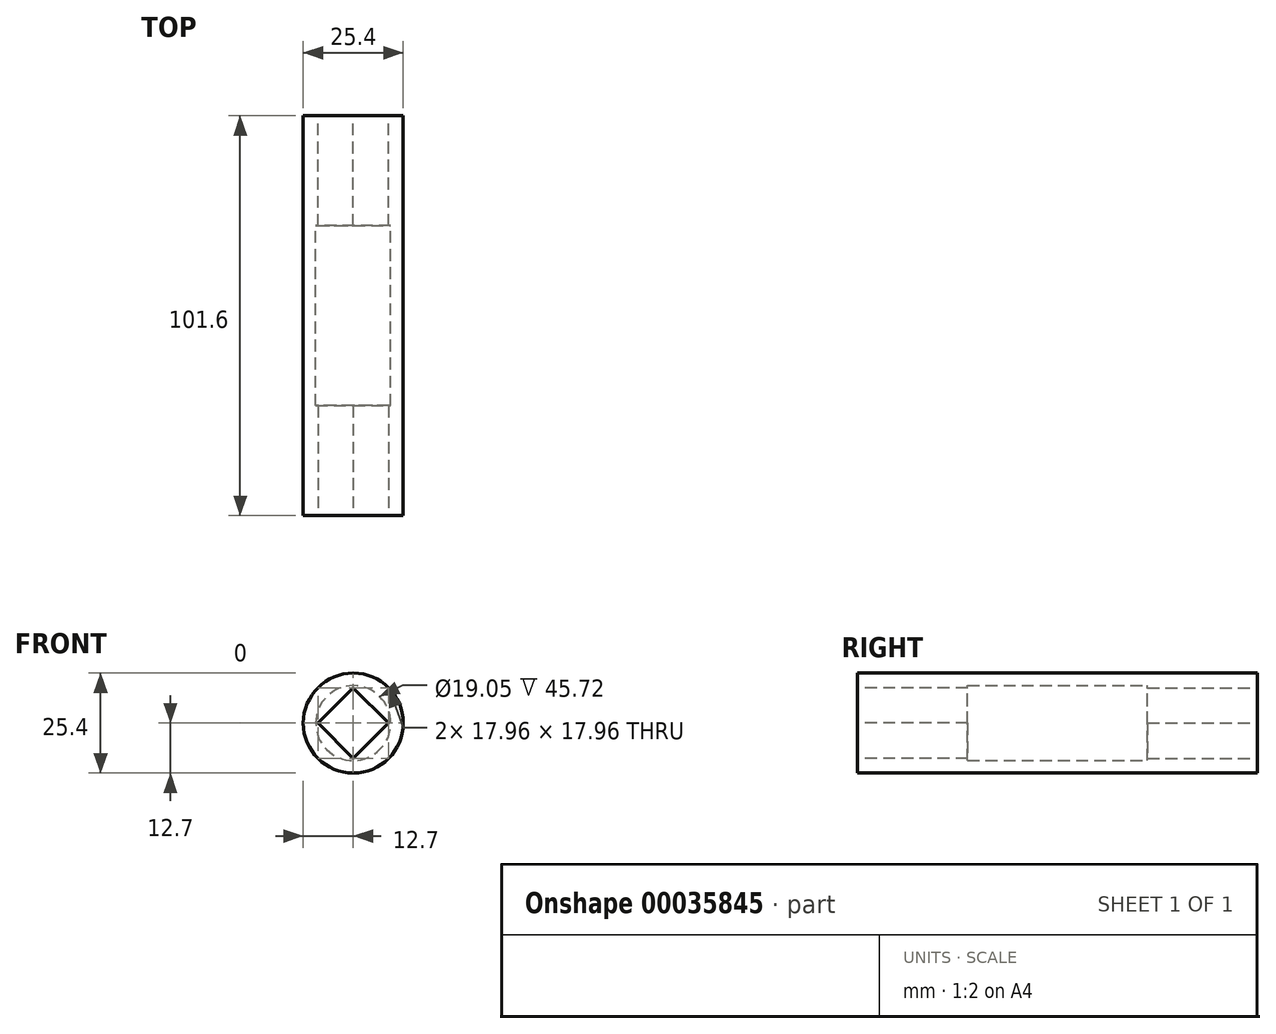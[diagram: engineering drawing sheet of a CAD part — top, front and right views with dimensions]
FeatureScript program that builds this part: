
annotation { "Feature Type Name" : "Feature", "Feature Type Description" : "" }
export const myFeature = defineFeature(function(context is Context, id is Id, definition is map)
    precondition{}
    {
        {
            var Q0;
            Q0=qCreatedBy(makeId("Front.planeOp"),FACE);
            var sketch = newSketch(context, id + "F0", { "sketchPlane" : qUnion([Q0])});
            skCircle(sketch, "E0", {"center": v(0, 0) * mm, "radius": 12.7 * mm});
            skSolve(sketch);
        }
        {
            var Q0;
            Q0=makeQuery(id+"F0.imprint","IMPRINT",FACE,{"disambiguationData":[TD([[makeQuery(id+"F0.imprint","IMPRINT",EDGE,{"derivedFrom":sQuery(id+"F0.wireOp",EDGE,"E0")}),1.0]])]});
            extrude(context, id + "F1", {"entities" : qUnion([Q0]), "depth" : 101.6 * mm});
        }
        {
            var Q0;
            Q0=makeQuery(id+"F1.opExtrude","CAP_FACE",FACE,{"disambiguationData":[OSD([sQuery(id+"F0.wireOp",EDGE,"E0")])],"isStart":false});
            var sketch = newSketch(context, id + "F2", { "sketchPlane" : qUnion([Q0])});
            skLineSegment(sketch, "E1.rect.bottom", {"start": v(8.98, 0) * mm, "end": v(0, -8.98) * mm});
            skLineSegment(sketch, "E1.rect.top", {"start": v(0, 8.98) * mm, "end": v(-8.98, 0) * mm});
            skLineSegment(sketch, "E1.rect.left", {"start": v(8.98, 0) * mm, "end": v(0, 8.98) * mm});
            skLineSegment(sketch, "E1.rect.right", {"start": v(0, -8.98) * mm, "end": v(-8.98, 0) * mm});
            skPoint(sketch, "E1.rect.middle", {"position": v(0, 0) * mm});
            skLineSegment(sketch, "E2", {"start": v(0, 8.82) * mm, "end": v(0, -11.14) * mm, "construction": true});
            skSolve(sketch);
        }
        {
            var Q0;
            Q0 = qSketchRegion(id + "F2", true);
            extrude(context, id + "F3", {"entities" : qUnion([Q0]), "operationType" : NewBodyOperationType.REMOVE, "oppositeDirection" : true, "depth" : 27.94 * mm});
        }
        {
            var Q0;
            Q0=makeQuery(id+"F1.opExtrude","CAP_FACE",FACE,{"disambiguationData":[OSD([sQuery(id+"F0.wireOp",EDGE,"E0")])],"isStart":true});
            var sketch = newSketch(context, id + "F4", { "sketchPlane" : qUnion([Q0])});
            skLineSegment(sketch, "E3.rect.bottom", {"start": v(8.98, 0) * mm, "end": v(0, -8.98) * mm});
            skLineSegment(sketch, "E3.rect.top", {"start": v(0, 8.98) * mm, "end": v(-8.98, 0) * mm});
            skLineSegment(sketch, "E3.rect.left", {"start": v(8.98, 0) * mm, "end": v(0, 8.98) * mm});
            skLineSegment(sketch, "E3.rect.right", {"start": v(0, -8.98) * mm, "end": v(-8.98, 0) * mm});
            skPoint(sketch, "E3.rect.middle", {"position": v(0, 0) * mm});
            skLineSegment(sketch, "E4", {"start": v(0, 9.26) * mm, "end": v(0, -9.94) * mm, "construction": true});
            skSolve(sketch);
        }
        {
            var Q0;
            Q0=makeQuery(id+"F4.imprint","IMPRINT",FACE,{"disambiguationData":[TD([[makeQuery(id+"F4.imprint","IMPRINT",EDGE,{"derivedFrom":sQuery(id+"F4.wireOp",EDGE,"E3.rect.bottom")}),-1.0]])]});
            extrude(context, id + "F5", {"entities" : qUnion([Q0]), "operationType" : NewBodyOperationType.REMOVE, "oppositeDirection" : true, "depth" : 27.94 * mm});
        }
        {
            var Q0;
            Q0=qCreatedBy(makeId("Front.planeOp"),FACE);
            cPlane(context, id + "F6", {"entities" : qUnion([Q0]), "cplaneType" : CPlaneType.OFFSET, "offset" : 27.94 * mm, "width" : 152.4 * mm, "height" : 152.4 * mm});
        }
        {
            var Q0;
            Q0=qCreatedBy(id+"F6.planeOp",FACE);
            var sketch = newSketch(context, id + "F7", { "sketchPlane" : qUnion([Q0])});
            skCircle(sketch, "E5", {"center": v(0, 0) * mm, "radius": 9.53 * mm});
            skSolve(sketch);
        }
        {
            var Q0;
            Q0 = qSketchRegion(id + "F7", true);
            extrude(context, id + "F8", {"entities" : qUnion([Q0]), "operationType" : NewBodyOperationType.REMOVE, "depth" : 45.72 * mm});
        }
    });
